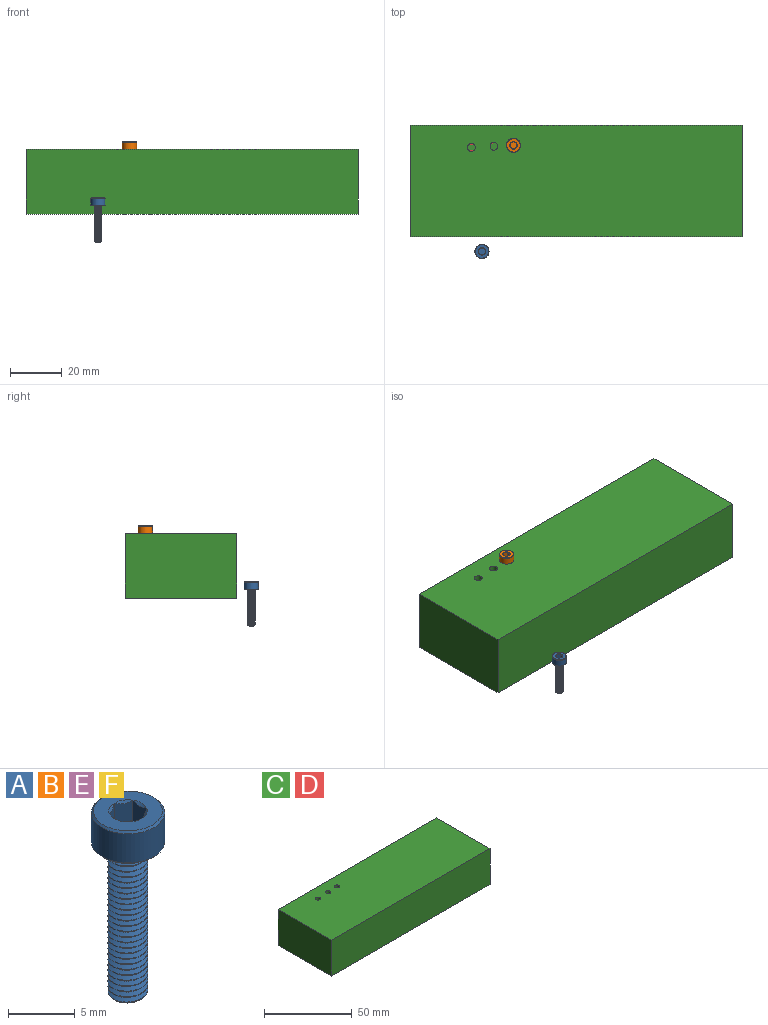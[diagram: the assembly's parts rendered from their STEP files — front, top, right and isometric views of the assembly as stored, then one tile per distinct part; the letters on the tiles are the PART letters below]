
ASSEMBLY  parts=6 mates=1
PART A: 53 faces, bbox 6x6x17.6 mm
  f0: cylinder r=1.5mm len=3mm, axis (0,0,-1), area 0.3mm2, adj f1,f28,f29,f31,f32
  f1: cylinder r=1.5mm len=3mm, axis (0,0,-1), area 0.6mm2, adj f0,f2,f28,f29
  f2: cylinder r=1.5mm len=3mm, axis (0,0,-1), area 0.6mm2, adj f1,f3,f28,f29
  f3: cylinder r=1.5mm len=3mm, axis (0,0,-1), area 0.6mm2, adj f2,f4,f28,f29
  f4: cylinder r=1.5mm len=3mm, axis (0,0,-1), area 0.6mm2, adj f3,f5,f28,f29
  f5: cylinder r=1.5mm len=3mm, axis (0,0,-1), area 0.6mm2, adj f4,f6,f28,f29
  f6: cylinder r=1.5mm len=3mm, axis (0,0,-1), area 0.6mm2, adj f5,f7,f28,f29
  f7: cylinder r=1.5mm len=3mm, axis (0,0,-1), area 0.6mm2, adj f6,f8,f28,f29
  f8: cylinder r=1.5mm len=3mm, axis (0,0,-1), area 0.6mm2, adj f7,f9,f28,f29
  f9: cylinder r=1.5mm len=3mm, axis (0,0,-1), area 0.6mm2, adj f8,f10,f28,f29
  f10: cylinder r=1.5mm len=3mm, axis (0,0,-1), area 0.6mm2, adj f9,f11,f28,f29
  f11: cylinder r=1.5mm len=3mm, axis (0,0,-1), area 0.6mm2, adj f10,f12,f28,f29
  f12: cylinder r=1.5mm len=3mm, axis (0,0,-1), area 0.6mm2, adj f11,f13,f28,f29
  f13: cylinder r=1.5mm len=3mm, axis (0,0,-1), area 0.6mm2, adj f12,f14,f28,f29
  f14: cylinder r=1.5mm len=3mm, axis (0,0,-1), area 0.6mm2, adj f13,f15,f28,f29
  f15: cylinder r=1.5mm len=3mm, axis (0,0,-1), area 0.6mm2, adj f14,f16,f28,f29
  f16: cylinder r=1.5mm len=3mm, axis (0,0,-1), area 0.6mm2, adj f15,f17,f28,f29
  f17: cylinder r=1.5mm len=3mm, axis (0,0,-1), area 0.6mm2, adj f16,f18,f28,f29
  f18: cylinder r=1.5mm len=3mm, axis (0,0,-1), area 0.6mm2, adj f17,f19,f28,f29
  f19: cylinder r=1.5mm len=3mm, axis (0,0,-1), area 0.6mm2, adj f18,f20,f28,f29
  f20: cylinder r=1.5mm len=3mm, axis (0,0,-1), area 0.6mm2, adj f19,f21,f28,f29
  f21: cylinder r=1.5mm len=3mm, axis (0,0,-1), area 0.6mm2, adj f20,f22,f28,f29
  f22: cylinder r=1.5mm len=3mm, axis (0,0,-1), area 0.6mm2, adj f21,f23,f28,f29
  f23: cylinder r=1.5mm len=3mm, axis (0,0,-1), area 0.6mm2, adj f22,f24,f28,f29
  f24: cylinder r=1.5mm len=3mm, axis (0,0,-1), area 0.6mm2, adj f23,f25,f28,f29
  f25: cylinder r=1.5mm len=3mm, axis (0,0,-1), area 0.6mm2, adj f24,f26,f28,f29
  f26: cylinder r=1.5mm len=3mm, axis (0,0,-1), area 0.6mm2, adj f25,f27,f28,f29
  f27: cylinder r=1.5mm len=3mm, axis (0,0,-1), area 1.4mm2, adj f26,f28,f29,f36,f52
  f28: bspline ~14.1x3.46mm, area 84.7mm2, adj f0,f1,f2,f3,f4,f5,f6,f7
  f29: bspline ~13.85x3.46mm, area 85.3mm2, adj f0,f1,f2,f3,f4,f5,f6,f7
  f30: cylinder r=1.18mm len=13.56mm, axis (0,0,1), area -3.9mm2, adj f28,f29,f31,f52
  f31: cone r=0.92mm half-angle=55deg, axis (0,0,1), area 3.5mm2, adj f0,f28,f30,f32,f33
  f32: cone r=0.92mm half-angle=55deg, axis (0,0,1), area 0.1mm2, adj f0,f29,f31
  f33: plane 1.84x1.84mm, normal (0,0,-1), area 2.7mm2, adj f31
  f34: cylinder r=2.75mm len=5.5mm, axis (0,0,-1), area 46.1mm2, adj f50,f51
  f35: plane 5.17x5.17mm, normal (0,0,1), area 14.4mm2, adj f37,f38,f39,f40,f41,f42,f50
  f36: plane 5.17x5.17mm, normal (0,0,-1), area 13.9mm2, adj f27,f51
  f37: cone r=1.44mm half-angle=45deg, axis (0,0,1), area 0mm2, adj f35,f44
  f38: cone r=1.44mm half-angle=45deg, axis (0,0,1), area 0mm2, adj f35,f45
  f39: cone r=1.44mm half-angle=45deg, axis (0,0,1), area 0mm2, adj f35,f46
  f40: cone r=1.44mm half-angle=45deg, axis (0,0,1), area 0mm2, adj f35,f47
  f41: cone r=1.44mm half-angle=45deg, axis (0,0,1), area 0mm2, adj f35,f48
  f42: cone r=1.44mm half-angle=45deg, axis (0,0,1), area 0mm2, adj f35,f49
  f43: plane 2.89x2.5mm, normal (0,0,1), area 5.4mm2, adj f44,f45,f46,f47,f48,f49
  f44: plane 2.42x1.8mm, normal (-0.5,0.87,0), area 2.5mm2, adj f37,f43,f45,f49
  f45: plane 2.42x1.99mm, normal (-1,0,0), area 2.5mm2, adj f38,f43,f44,f46
  f46: plane 2.42x1.8mm, normal (-0.5,-0.87,0), area 2.5mm2, adj f39,f43,f45,f47
  f47: plane 2.42x1.8mm, normal (0.5,-0.87,0), area 2.5mm2, adj f40,f43,f46,f48
  f48: plane 2.42x1.99mm, normal (1,0,0), area 2.5mm2, adj f41,f43,f47,f49
  f49: plane 2.42x1.8mm, normal (0.5,0.87,0), area 2.5mm2, adj f42,f43,f44,f48
  f50: cone r=2.58mm half-angle=45deg, axis (0,0,-1), area 3.9mm2, adj f34,f35
  f51: cone r=2.75mm half-angle=45deg, axis (0,0,1), area 3.9mm2, adj f34,f36
  f52: cone r=1.5mm half-angle=67.5deg, axis (0,0,1), area 1.5mm2, adj f27,f28,f29,f30
PART B: same geometry as A
PART C: 12 faces, bbox 127.7x42.9x25 mm
  f0: plane 127.73x25mm, normal (0,1,0), area 3193.1mm2, adj f1,f3,f4,f5
  f1: plane 42.85x25mm, normal (-1,0,0), area 1071.3mm2, adj f0,f2,f4,f5
  f2: plane 127.73x25mm, normal (0,-1,0), area 3193.1mm2, adj f1,f3,f4,f5
  f3: plane 42.85x25mm, normal (1,0,0), area 1071.3mm2, adj f0,f2,f4,f5
  f4: plane 127.73x42.85mm, normal (0,0,1), area 5452.3mm2, adj f0,f1,f2,f3,f6,f8,f10
  f5: plane 127.73x42.85mm, normal (0,0,-1), area 5473.5mm2, adj f0,f1,f2,f3
  f6: cylinder r=1.5mm len=15mm, axis (0,0,1), area 141.4mm2, adj f4,f7
  f7: plane 3x3mm, normal (0,0,1), area 7.1mm2, adj f6
  f8: cylinder r=1.5mm len=15mm, axis (0,0,1), area 141.4mm2, adj f4,f9
  f9: plane 3x3mm, normal (0,0,1), area 7.1mm2, adj f8
  f10: cylinder r=1.5mm len=15mm, axis (0,0,1), area 141.4mm2, adj f4,f11
  f11: plane 3x3mm, normal (0,0,1), area 7.1mm2, adj f10
PART D: same geometry as C
PART E: same geometry as A
PART F: same geometry as A
PLACE A t=(-30.5,-6.8,16.22)mm
PLACE B t=(-18.37,33.98,37.79)mm
PLACE C t=(5.67,20.25,12.95)mm
PLACE D t=(5.67,20.25,12.95)mm
PLACE E t=(-30.5,-6.8,16.22)mm
PLACE F t=(-30.5,-6.8,16.22)mm
MATE fastened B.f34 <-> C.f6  axis (0,0,1) through (-18.37,33.98,37.95)mm
